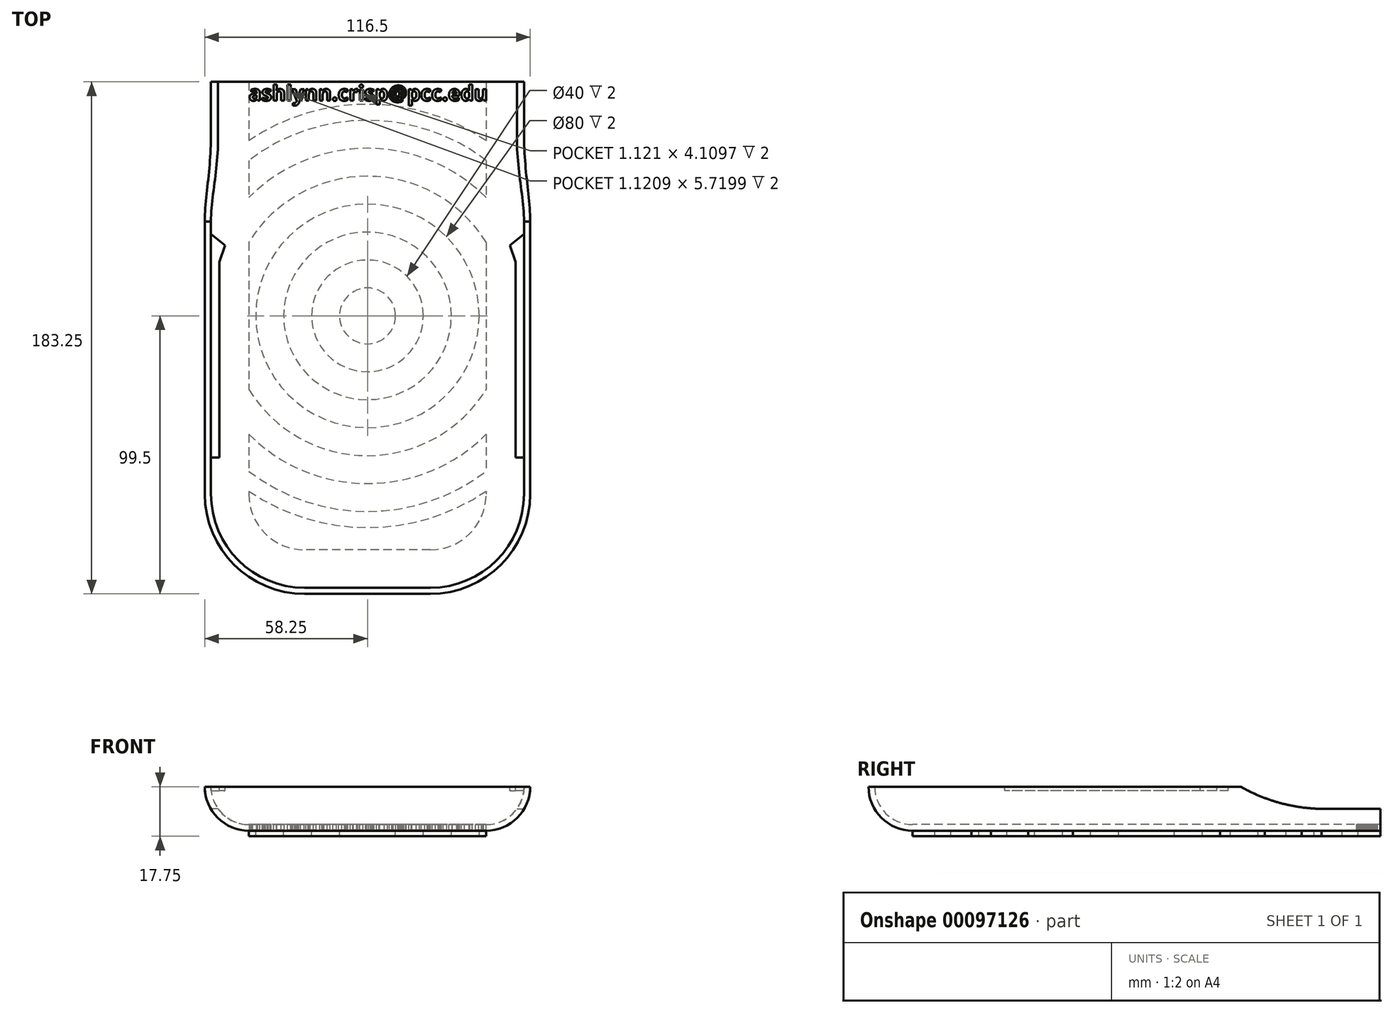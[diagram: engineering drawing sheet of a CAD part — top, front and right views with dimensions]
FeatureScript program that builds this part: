
annotation { "Feature Type Name" : "Feature", "Feature Type Description" : "" }
export const myFeature = defineFeature(function(context is Context, id is Id, definition is map)
    precondition{}
    {
        {
            var Q0;
            Q0=qCreatedBy(makeId("Right.planeOp"),FACE);
            var sketch = newSketch(context, id + "F0", { "sketchPlane" : qUnion([Q0])});
            skArc(sketch, "E0", {"start": v(-33.55, 13.55) * mm, "mid": v(-29.58, 3.97) * mm, "end": v(-20, 0) * mm});
            skArc(sketch, "E1", {"start": v(-35.75, 13.55) * mm, "mid": v(-31.14, 2.41) * mm, "end": v(-20, -2.2) * mm});
            skLineSegment(sketch, "E2", {"start": v(0, 0) * mm, "end": v(0, -24.6) * mm, "construction": true});
            skLineSegment(sketch, "E3", {"start": v(-35.75, 13.55) * mm, "end": v(-33.55, 13.55) * mm});
            skLineSegment(sketch, "E4", {"start": v(-20, 0) * mm, "end": v(-20, -2.2) * mm});
            skLineSegment(sketch, "E5", {"start": v(-29.58, 3.97) * mm, "end": v(-31.14, 2.41) * mm, "construction": true});
            skSolve(sketch);
        }
        {
            var Q0;
            Q0=makeQuery(id+"F0.imprint","IMPRINT",FACE,{"disambiguationData":[TD([[makeQuery(id+"F0.imprint","IMPRINT",EDGE,{"derivedFrom":sQuery(id+"F0.wireOp",EDGE,"E0")}),-1.0]])]});
            var Q1;
            Q1=sQuery(id+"F0.wireOp",EDGE,"E2");
            revolve(context, id + "F1", {"entities" : qUnion([Q0]), "axis" : qUnion([Q1]), "revolveType" : RevolveType.ONE_DIRECTION, "angle" : 90 * degree});
        }
        {
            var Q0;
            Q0=makeQuery(id+"F1.opRevolve","CAP_FACE",FACE,{"disambiguationData":[OSD([sQuery(id+"F0.wireOp",EDGE,"E0"),sQuery(id+"F0.wireOp",EDGE,"E1"),sQuery(id+"F0.wireOp",EDGE,"E3"),sQuery(id+"F0.wireOp",EDGE,"E4")])],"isStart":false});
            extrude(context, id + "F2", {"entities" : qUnion([Q0]), "operationType" : NewBodyOperationType.ADD, "depth" : 147.5 * mm});
        }
        {
            var Q0;
            Q0=makeQuery(id+"F1.opRevolve","CAP_FACE",FACE,{"disambiguationData":[OSD([sQuery(id+"F0.wireOp",EDGE,"E0"),sQuery(id+"F0.wireOp",EDGE,"E1"),sQuery(id+"F0.wireOp",EDGE,"E3"),sQuery(id+"F0.wireOp",EDGE,"E4")])],"isStart":true});
            extrude(context, id + "F3", {"entities" : qUnion([Q0]), "operationType" : NewBodyOperationType.ADD, "depth" : 22.5 * mm});
        }
        {
            var Q0;
            Q0=makeQuery(id+"F2.opExtrude","SWEPT_FACE",FACE,{"disambiguationData":[OSD([sQuery(id+"F0.wireOp",EDGE,"E4")])]});
            var Q1;
            Q1=makeQuery(id+"F3.opExtrude","CAP_FACE",FACE,{"disambiguationData":[OSD([sQuery(id+"F0.wireOp",EDGE,"E0"),sQuery(id+"F0.wireOp",EDGE,"E1"),sQuery(id+"F0.wireOp",EDGE,"E3"),sQuery(id+"F0.wireOp",EDGE,"E4")])],"isStart":false});
            extrude(context, id + "F4", {"entities" : qUnion([Q0]), "operationType" : NewBodyOperationType.ADD, "endBound" : BoundingType.UP_TO_SURFACE, "endBoundEntityFace" : qUnion([Q1]), "depth" : 25 * mm});
        }
        {
            var Q0;
            {var subQ0=sQuery(id+"F0.wireOp",EDGE,"E4");Q0=makeQuery(id+"F4.opExtrude","SWEPT_FACE",FACE,{"disambiguationData":[OSD([subQ0]),TDD([makeQuery(id+"F2.boolean.opBoolean","MERGE",EDGE,{"derivedFrom":[makeQuery(id+"F1.opRevolve","CAP_EDGE",EDGE,{"disambiguationData":[OSD([subQ0])],"isStart":false}),makeQuery(id+"F2.opExtrude","CAP_EDGE",EDGE,{"disambiguationData":[OSD([subQ0])],"isStart":true})]})])]});}
            var Q1;
            Q1=makeQuery(id+"F1.opRevolve","SWEPT_BODY",BODY,{"disambiguationData":[OSD([sQuery(id+"F0.wireOp",EDGE,"E0"),sQuery(id+"F0.wireOp",EDGE,"E1"),sQuery(id+"F0.wireOp",EDGE,"E3"),sQuery(id+"F0.wireOp",EDGE,"E4")])]});
            extrude(context, id + "F5", {"entities" : qUnion([Q0]), "operationType" : NewBodyOperationType.ADD, "endBound" : BoundingType.UP_TO_BODY, "endBoundEntityBody" : qUnion([Q1]), "depth" : 25 * mm});
        }
        {
            var Q0;
            Q0=makeQuery(id+"F2.opExtrude","SWEPT_EDGE",EDGE,{"disambiguationData":[OSD([sQuery(id+"F0.wireOp",EDGE,"E1"),sQuery(id+"F0.wireOp",EDGE,"E3")])]});
            cPlane(context, id + "F6", {"entities" : qUnion([Q0]), "cplaneType" : CPlaneType.LINE_ANGLE, "offset" : 150 * mm, "angle" : 90 * degree, "width" : 150 * mm, "height" : 150 * mm});
        }
        {
            var Q0;
            Q0=qCreatedBy(id+"F6.planeOp",FACE);
            var sketch = newSketch(context, id + "F7", { "sketchPlane" : qUnion([Q0])});
            skLineSegment(sketch, "E6.0", {"start": v(147.5, 13.55) * mm, "end": v(0, 13.55) * mm});
            skLineSegment(sketch, "E7.0", {"start": v(147.5, 13.55) * mm, "end": v(147.5, -2.2) * mm});
            skLineSegment(sketch, "E8.0", {"start": v(147.5, -2.2) * mm, "end": v(0, -2.2) * mm});
            skArc(sketch, "E9", {"start": v(97.5, 13.55) * mm, "mid": v(111.98, 7.62) * mm, "end": v(127.5, 5.6) * mm});
            skLineSegment(sketch, "E10", {"start": v(147.5, 5.6) * mm, "end": v(127.5, 5.6) * mm});
            skPoint(sketch, "E11", {"position": v(147.5, 5.68) * mm});
            skSolve(sketch);
        }
        {
            var Q0;
            {var subQ3=sQuery(id+"F7.wireOp",EDGE,"E9");Q0=makeQuery(id+"F7.imprint","IMPRINT",FACE,{"disambiguationData":[TD([[makeQuery(id+"F7.imprint","IMPRINT",EDGE,{"derivedFrom":subQ3}),1.0]])]});}
            var Q1;
            Q1=makeQuery(id+"F2.opExtrude","SWEPT_FACE",FACE,{"disambiguationData":[OSD([sQuery(id+"F0.wireOp",EDGE,"E0")])]});
            var Q2;
            Q2=makeQuery(id+"F1.opRevolve","SWEPT_BODY",BODY,{"disambiguationData":[OSD([sQuery(id+"F0.wireOp",EDGE,"E0"),sQuery(id+"F0.wireOp",EDGE,"E1"),sQuery(id+"F0.wireOp",EDGE,"E3"),sQuery(id+"F0.wireOp",EDGE,"E4")])]});
            extrude(context, id + "F8", {"entities" : qUnion([Q0]), "operationType" : NewBodyOperationType.REMOVE, "endBound" : BoundingType.THROUGH_ALL, "endBoundEntityFace" : qUnion([Q1]), "endBoundEntityBody" : qUnion([Q2]), "depth" : 25 * mm});
        }
        {
            var Q0;
            Q0=makeQuery(id+"F1.opRevolve","SWEPT_BODY",BODY,{"disambiguationData":[OSD([sQuery(id+"F0.wireOp",EDGE,"E0"),sQuery(id+"F0.wireOp",EDGE,"E1"),sQuery(id+"F0.wireOp",EDGE,"E3"),sQuery(id+"F0.wireOp",EDGE,"E4")])]});
            var Q1;
            {var subQ0=sQuery(id+"F0.wireOp",EDGE,"E4");var subQ1=sQuery(id+"F0.wireOp",EDGE,"E3");var subQ2=sQuery(id+"F0.wireOp",EDGE,"E1");var subQ3=sQuery(id+"F0.wireOp",EDGE,"E0");Q1=makeQuery(id+"F5.boolean.opBoolean","MERGE",FACE,{"derivedFrom":[makeQuery(id+"F3.opExtrude","CAP_FACE",FACE,{"disambiguationData":[OSD([subQ3,subQ2,subQ1,subQ0])],"isStart":false}),makeQuery(id+"F4.opExtrude","CAP_FACE",FACE,{"disambiguationData":[OSD([subQ3,subQ2,subQ1,subQ0])],"isStart":false}),makeQuery(id+"F5.opExtrude","SWEPT_FACE",FACE,{"disambiguationData":[OSD([subQ3,subQ2,subQ1,subQ0])]})]});}
            mirror(context, id + "F9", {"operationType" : NewBodyOperationType.ADD, "entities" : qUnion([Q0]), "mirrorPlane" : qUnion([Q1])});
        }
        {
            var Q0;
            {var subQ0=sQuery(id+"F0.wireOp",EDGE,"E4");var subQ1=sQuery(id+"F0.wireOp",EDGE,"E1");var subQ2=makeQuery(id+"F5.boolean.opBoolean","MERGE",FACE,{"derivedFrom":[makeQuery(id+"F4.opExtrude","SWEPT_FACE",FACE,{"disambiguationData":[OSD([subQ1,subQ0])]}),makeQuery(id+"F5.opExtrude","SWEPT_FACE",FACE,{"disambiguationData":[OSD([subQ1,subQ0])]})]});Q0=makeQuery(id+"F9.boolean.opBoolean","MERGE",FACE,{"derivedFrom":[subQ2,makeQuery(id+"F9.opPattern","COPY",FACE,{"derivedFrom":subQ2,"instanceName":"1"})]});}
            var sketch = newSketch(context, id + "F10", { "sketchPlane" : qUnion([Q0])});
            skPoint(sketch, "E12", {"position": v(22.5, -63.75) * mm});
            skCircle(sketch, "E13", {"center": v(22.5, -63.75) * mm, "radius": 10 * mm});
            skCircle(sketch, "E14", {"center": v(22.5, -63.75) * mm, "radius": 20 * mm});
            skCircle(sketch, "E15", {"center": v(22.5, -63.75) * mm, "radius": 30 * mm});
            skCircle(sketch, "E16", {"center": v(22.5, -63.75) * mm, "radius": 40 * mm});
            skArc(sketch, "E17", {"start": v(-20, -90.09) * mm, "mid": v(22.5, -113.75) * mm, "end": v(65, -90.09) * mm});
            skArc(sketch, "E18", {"start": v(-20, -106.1) * mm, "mid": v(22.5, -123.75) * mm, "end": v(65, -106.1) * mm});
            skLineSegment(sketch, "E19", {"start": v(32.5, -63.75) * mm, "end": v(12.5, -63.75) * mm, "construction": true});
            skLineSegment(sketch, "E20", {"start": v(32.5, -63.75) * mm, "end": v(42.5, -63.75) * mm, "construction": true});
            skLineSegment(sketch, "E21", {"start": v(42.5, -63.75) * mm, "end": v(52.5, -63.75) * mm, "construction": true});
            skLineSegment(sketch, "E22", {"start": v(52.5, -63.75) * mm, "end": v(62.5, -63.75) * mm, "construction": true});
            skLineSegment(sketch, "E23", {"start": v(62.5, -63.75) * mm, "end": v(72.5, -63.75) * mm, "construction": true});
            skLineSegment(sketch, "E24", {"start": v(72.5, -63.75) * mm, "end": v(82.5, -63.75) * mm, "construction": true});
            skArc(sketch, "E25", {"start": v(-20, -119.37) * mm, "mid": v(22.5, -133.75) * mm, "end": v(65, -119.37) * mm});
            skLineSegment(sketch, "E26", {"start": v(82.5, -63.75) * mm, "end": v(92.5, -63.75) * mm, "construction": true});
            skLineSegment(sketch, "E27", {"start": v(92.5, -63.75) * mm, "end": v(102.5, -63.75) * mm, "construction": true});
            skLineSegment(sketch, "E28", {"start": v(102.5, -63.75) * mm, "end": v(112.5, -63.75) * mm, "construction": true});
            skLineSegment(sketch, "E29", {"start": v(112.5, -63.75) * mm, "end": v(122.5, -63.75) * mm, "construction": true});
            skLineSegment(sketch, "E30.0.0", {"start": v(-20, -147.5) * mm, "end": v(65, -147.5) * mm});
            skLineSegment(sketch, "E30.0.1", {"start": v(65, -147.5) * mm, "end": v(65, 0) * mm});
            skArc(sketch, "E30.0.2", {"start": v(65, 0) * mm, "mid": v(59.14, 14.14) * mm, "end": v(45, 20) * mm});
            skLineSegment(sketch, "E30.0.3", {"start": v(45, 20) * mm, "end": v(0, 20) * mm});
            skArc(sketch, "E30.0.4", {"start": v(0, 20) * mm, "mid": v(-14.14, 14.14) * mm, "end": v(-20, 0) * mm});
            skLineSegment(sketch, "E30.0.5", {"start": v(-20, 0) * mm, "end": v(-20, -147.5) * mm});
            skArc(sketch, "E31.trimOffspring", {"start": v(65, -8.13) * mm, "mid": v(22.5, 6.25) * mm, "end": v(-20, -8.13) * mm});
            skArc(sketch, "E32.trimOffspring", {"start": v(65, -21.4) * mm, "mid": v(22.5, -3.75) * mm, "end": v(-20, -21.4) * mm});
            skArc(sketch, "E33.trimOffspring", {"start": v(65, -37.41) * mm, "mid": v(22.5, -13.75) * mm, "end": v(-20, -37.41) * mm});
            skArc(sketch, "E34", {"start": v(64.53, 4.32) * mm, "mid": v(22.5, 16.25) * mm, "end": v(-19.53, 4.32) * mm});
            skCircle(sketch, "E35", {"center": v(22.5, -63.75) * mm, "radius": 75.75 * mm});
            skPoint(sketch, "E36", {"position": v(22.5, -147.5) * mm});
            skPoint(sketch, "E37", {"position": v(22.5, -139.5) * mm});
            skSolve(sketch);
        }
        {
            var Q0;
            Q0=makeQuery(id+"F10.imprint","IMPRINT",FACE,{"disambiguationData":[TD([[makeQuery(id+"F10.imprint","IMPRINT",EDGE,{"derivedFrom":sQuery(id+"F10.wireOp",EDGE,"E13")}),1.0]])]});
            var Q1;
            Q1=makeQuery(id+"F10.imprint","IMPRINT",FACE,{"disambiguationData":[TD([[makeQuery(id+"F10.imprint","IMPRINT",EDGE,{"derivedFrom":sQuery(id+"F10.wireOp",EDGE,"E14")}),-1.0]])]});
            var Q2;
            Q2=makeQuery(id+"F10.imprint","IMPRINT",FACE,{"disambiguationData":[TD([[makeQuery(id+"F10.imprint","IMPRINT",EDGE,{"derivedFrom":sQuery(id+"F10.wireOp",EDGE,"E16")}),-1.0]])]});
            var Q3;
            {var subQ0=sQuery(id+"F10.wireOp",EDGE,"E31.trimOffspring");Q3=makeQuery(id+"F10.imprint","IMPRINT",FACE,{"disambiguationData":[TD([[makeQuery(id+"F10.imprint","IMPRINT",EDGE,{"derivedFrom":subQ0}),1.0]])]});}
            var Q4;
            {var subQ0=sQuery(id+"F10.wireOp",EDGE,"E18");Q4=makeQuery(id+"F10.imprint","IMPRINT",FACE,{"disambiguationData":[TD([[makeQuery(id+"F10.imprint","IMPRINT",EDGE,{"derivedFrom":subQ0}),-1.0]])]});}
            var Q5;
            {var subQ0=sQuery(id+"F10.wireOp",EDGE,"E30.0.0");Q5=makeQuery(id+"F10.imprint","IMPRINT",FACE,{"disambiguationData":[TD([[makeQuery(id+"F10.imprint","IMPRINT",EDGE,{"derivedFrom":subQ0}),-1.0]])]});}
            var Q6;
            {var subQ8=sQuery(id+"F10.wireOp",EDGE,"E34");Q6=makeQuery(id+"F10.imprint","IMPRINT",FACE,{"disambiguationData":[TD([[makeQuery(id+"F10.imprint","IMPRINT",EDGE,{"derivedFrom":subQ8}),1.0]])]});}
            var Q7;
            {var subQ0=sQuery(id+"F10.wireOp",EDGE,"E30.0.3");Q7=makeQuery(id+"F10.imprint","IMPRINT",FACE,{"disambiguationData":[TD([[makeQuery(id+"F10.imprint","IMPRINT",EDGE,{"derivedFrom":subQ0}),1.0]])]});}
            extrude(context, id + "F11", {"entities" : qUnion([Q0, Q1, Q2, Q3, Q4, Q5, Q6, Q7]), "depth" : 2 * mm});
        }
        {
            var Q0;
            {var subQ0=sQuery(id+"F0.wireOp",EDGE,"E4");var subQ1=sQuery(id+"F0.wireOp",EDGE,"E0");var subQ2=makeQuery(id+"F5.boolean.opBoolean","MERGE",FACE,{"derivedFrom":[makeQuery(id+"F4.opExtrude","SWEPT_FACE",FACE,{"disambiguationData":[OSD([subQ1,subQ0])]}),makeQuery(id+"F5.opExtrude","SWEPT_FACE",FACE,{"disambiguationData":[OSD([subQ1,subQ0])]})]});Q0=makeQuery(id+"F9.boolean.opBoolean","MERGE",FACE,{"derivedFrom":[subQ2,makeQuery(id+"F9.opPattern","COPY",FACE,{"derivedFrom":subQ2,"instanceName":"1"})]});}
            var sketch = newSketch(context, id + "F12", { "sketchPlane" : qUnion([Q0])});
            skLineSegment(sketch, "E38.0.1", {"start": v(-20, 126.45) * mm, "end": v(-20, 147.5) * mm});
            skLineSegment(sketch, "E38.0.2", {"start": v(-20, 147.5) * mm, "end": v(65, 147.5) * mm});
            skLineSegment(sketch, "E38.0.3", {"start": v(65, 147.5) * mm, "end": v(65, 126.45) * mm});
            skText(sketch, "E39", { "text": "<email>", "fontName": "OpenSans-Bold.ttf"});
            skPoint(sketch, "E40", {"position": v(22.5, 147.5) * mm});
            skPoint(sketch, "E41", {"position": v(22.5, 139.5) * mm});
            skLineSegment(sketch, "E42", {"start": v(22.5, 147.5) * mm, "end": v(22.5, 139.5) * mm, "construction": true});
            skPoint(sketch, "E43", {"position": v(22.5, 143.5) * mm});
            skArc(sketch, "E44.0.0", {"start": v(65, 126.45) * mm, "mid": v(22.5, 139.5) * mm, "end": v(-20, 126.45) * mm});
            const initialGuessF12  = {"E39": [-0.02, 0.14079, 1, 0, 0.00542]};
            skSetInitialGuess(sketch, initialGuessF12);
            skSolve(sketch);
        }
        {
            var Q0;
            Q0=makeQuery(id+"F12.imprint","IMPRINT",FACE,{"disambiguationData":[TD([[makeQuery(id+"F12.imprint","IMPRINT",EDGE,{"derivedFrom":sQuery(id+"F12.wireOp",EDGE,"E39.sketch_text.stroke-0")}),-1.0]])]});
            var Q1;
            Q1=makeQuery(id+"F12.imprint","IMPRINT",FACE,{"disambiguationData":[TD([[makeQuery(id+"F12.imprint","IMPRINT",EDGE,{"derivedFrom":sQuery(id+"F12.wireOp",EDGE,"E39.sketch_text.stroke-25")}),-1.0]])]});
            var Q2;
            Q2=makeQuery(id+"F12.imprint","IMPRINT",FACE,{"disambiguationData":[TD([[makeQuery(id+"F12.imprint","IMPRINT",EDGE,{"derivedFrom":sQuery(id+"F12.wireOp",EDGE,"E39.sketch_text.stroke-51")}),-1.0]])]});
            var Q3;
            Q3=makeQuery(id+"F12.imprint","IMPRINT",FACE,{"disambiguationData":[TD([[makeQuery(id+"F12.imprint","IMPRINT",EDGE,{"derivedFrom":sQuery(id+"F12.wireOp",EDGE,"E39.sketch_text.stroke-68")}),-1.0]])]});
            var Q4;
            Q4=makeQuery(id+"F12.imprint","IMPRINT",FACE,{"disambiguationData":[TD([[makeQuery(id+"F12.imprint","IMPRINT",EDGE,{"derivedFrom":sQuery(id+"F12.wireOp",EDGE,"E39.sketch_text.stroke-72")}),-1.0]])]});
            var Q5;
            Q5=makeQuery(id+"F12.imprint","IMPRINT",FACE,{"disambiguationData":[TD([[makeQuery(id+"F12.imprint","IMPRINT",EDGE,{"derivedFrom":sQuery(id+"F12.wireOp",EDGE,"E39.sketch_text.stroke-89")}),-1.0]])]});
            var Q6;
            Q6=makeQuery(id+"F12.imprint","IMPRINT",FACE,{"disambiguationData":[TD([[makeQuery(id+"F12.imprint","IMPRINT",EDGE,{"derivedFrom":sQuery(id+"F12.wireOp",EDGE,"E39.sketch_text.stroke-106")}),-1.0]])]});
            var Q7;
            Q7=makeQuery(id+"F12.imprint","IMPRINT",FACE,{"disambiguationData":[TD([[makeQuery(id+"F12.imprint","IMPRINT",EDGE,{"derivedFrom":sQuery(id+"F12.wireOp",EDGE,"E39.sketch_text.stroke-123")}),-1.0]])]});
            var Q8;
            Q8=makeQuery(id+"F12.imprint","IMPRINT",FACE,{"disambiguationData":[TD([[makeQuery(id+"F12.imprint","IMPRINT",EDGE,{"derivedFrom":sQuery(id+"F12.wireOp",EDGE,"E39.sketch_text.stroke-131")}),-1.0]])]});
            var Q9;
            Q9=makeQuery(id+"F12.imprint","IMPRINT",FACE,{"disambiguationData":[TD([[makeQuery(id+"F12.imprint","IMPRINT",EDGE,{"derivedFrom":sQuery(id+"F12.wireOp",EDGE,"E39.sketch_text.stroke-145")}),-1.0]])]});
            var Q10;
            Q10=makeQuery(id+"F12.imprint","IMPRINT",FACE,{"disambiguationData":[TD([[makeQuery(id+"F12.imprint","IMPRINT",EDGE,{"derivedFrom":sQuery(id+"F12.wireOp",EDGE,"E39.sketch_text.stroke-158")}),-1.0]])]});
            var Q11;
            Q11=makeQuery(id+"F12.imprint","IMPRINT",FACE,{"disambiguationData":[TD([[makeQuery(id+"F12.imprint","IMPRINT",EDGE,{"derivedFrom":sQuery(id+"F12.wireOp",EDGE,"E39.sketch_text.stroke-163")}),-1.0]])]});
            var Q12;
            Q12=makeQuery(id+"F12.imprint","IMPRINT",FACE,{"disambiguationData":[TD([[makeQuery(id+"F12.imprint","IMPRINT",EDGE,{"derivedFrom":sQuery(id+"F12.wireOp",EDGE,"E39.sketch_text.stroke-167")}),-1.0]])]});
            var Q13;
            Q13=makeQuery(id+"F12.imprint","IMPRINT",FACE,{"disambiguationData":[TD([[makeQuery(id+"F12.imprint","IMPRINT",EDGE,{"derivedFrom":sQuery(id+"F12.wireOp",EDGE,"E39.sketch_text.stroke-193")}),-1.0]])]});
            var Q14;
            Q14=makeQuery(id+"F12.imprint","IMPRINT",FACE,{"disambiguationData":[TD([[makeQuery(id+"F12.imprint","IMPRINT",EDGE,{"derivedFrom":sQuery(id+"F12.wireOp",EDGE,"E39.sketch_text.stroke-216")}),-1.0]])]});
            var Q15;
            Q15=makeQuery(id+"F12.imprint","IMPRINT",FACE,{"disambiguationData":[TD([[makeQuery(id+"F12.imprint","IMPRINT",EDGE,{"derivedFrom":sQuery(id+"F12.wireOp",EDGE,"E39.sketch_text.stroke-260")}),-1.0]])]});
            var Q16;
            Q16=makeQuery(id+"F12.imprint","IMPRINT",FACE,{"disambiguationData":[TD([[makeQuery(id+"F12.imprint","IMPRINT",EDGE,{"derivedFrom":sQuery(id+"F12.wireOp",EDGE,"E39.sketch_text.stroke-283")}),-1.0]])]});
            var Q17;
            {var subQ6=sQuery(id+"F12.wireOp",EDGE,"E39.sketch_text.stroke-362");Q17=makeQuery(id+"F12.imprint","IMPRINT",FACE,{"disambiguationData":[TD([[makeQuery(id+"F12.imprint","IMPRINT",EDGE,{"derivedFrom":subQ6}),-1.0]])]});}
            var Q18;
            Q18=makeQuery(id+"F12.imprint","IMPRINT",FACE,{"disambiguationData":[TD([[makeQuery(id+"F12.imprint","IMPRINT",EDGE,{"derivedFrom":sQuery(id+"F12.wireOp",EDGE,"E39.sketch_text.stroke-297")}),-1.0]])]});
            var Q19;
            Q19=makeQuery(id+"F12.imprint","IMPRINT",FACE,{"disambiguationData":[TD([[makeQuery(id+"F12.imprint","IMPRINT",EDGE,{"derivedFrom":sQuery(id+"F12.wireOp",EDGE,"E39.sketch_text.stroke-319")}),-1.0]])]});
            var Q20;
            Q20=makeQuery(id+"F12.imprint","IMPRINT",FACE,{"disambiguationData":[TD([[makeQuery(id+"F12.imprint","IMPRINT",EDGE,{"derivedFrom":sQuery(id+"F12.wireOp",EDGE,"E39.sketch_text.stroke-339")}),-1.0]])]});
            var Q21;
            Q21=makeQuery(id+"F12.imprint","IMPRINT",FACE,{"disambiguationData":[TD([[makeQuery(id+"F12.imprint","IMPRINT",EDGE,{"derivedFrom":sQuery(id+"F12.wireOp",EDGE,"E39.sketch_text.stroke-311")}),-1.0]])]});
            extrude(context, id + "F13", {"entities" : qUnion([Q0, Q1, Q2, Q3, Q4, Q5, Q6, Q7, Q8, Q9, Q10, Q11, Q12, Q13, Q14, Q15, Q16, Q17, Q18, Q19, Q20, Q21]), "operationType" : NewBodyOperationType.REMOVE, "oppositeDirection" : true, "depth" : 2 * mm});
        }
        {
            var Q0;
            {var subQ0=sQuery(id+"F0.wireOp",EDGE,"E3");var subQ1=makeQuery(id+"F3.boolean.opBoolean","MERGE",FACE,{"derivedFrom":[makeQuery(id+"F2.boolean.opBoolean","MERGE",FACE,{"derivedFrom":[makeQuery(id+"F1.opRevolve","SWEPT_FACE",FACE,{"disambiguationData":[OSD([subQ0])]}),makeQuery(id+"F2.opExtrude","SWEPT_FACE",FACE,{"disambiguationData":[OSD([subQ0])]})]}),makeQuery(id+"F3.opExtrude","SWEPT_FACE",FACE,{"disambiguationData":[OSD([subQ0])]})]});Q0=makeQuery(id+"F9.boolean.opBoolean","MERGE",FACE,{"derivedFrom":[subQ1,makeQuery(id+"F9.opPattern","COPY",FACE,{"derivedFrom":subQ1,"instanceName":"1"})]});}
            var sketch = newSketch(context, id + "F14", { "sketchPlane" : qUnion([Q0])});
            skFitSpline(sketch, "E45.0.0", {"points": [v(-30.97, 127.5) * mm, v(-30.97, 126.2) * mm, v(-31, 124.88) * mm, v(-31.06, 123.55) * mm, v(-31.12, 122.3) * mm, v(-31.2, 121) * mm, v(-31.33, 119.65) * mm, v(-31.43, 118.45) * mm, v(-31.56, 117.16) * mm, v(-31.72, 115.78) * mm, v(-31.84, 114.73) * mm, v(-32, 113.45) * mm, v(-32.19, 111.95) * mm, v(-32.22, 111.69) * mm, v(-32.3, 111.06) * mm, v(-32.43, 110.07) * mm, v(-32.53, 109.3) * mm, v(-32.61, 108.69) * mm, v(-32.67, 108.21) * mm, v(-32.85, 106.8) * mm, v(-33, 105.58) * mm, v(-33.1, 104.56) * mm, v(-33.25, 103.26) * mm, v(-33.35, 102.07) * mm, v(-33.42, 101) * mm, v(-33.5, 99.74) * mm, v(-33.55, 98.57) * mm, v(-33.55, 97.5) * mm]});
            skLineSegment(sketch, "E45.0.1", {"start": v(-33.55, 97.5) * mm, "end": v(-33.55, 0) * mm});
            skLineSegment(sketch, "E45.0.2", {"start": v(-33.55, 0) * mm, "end": v(-20, 0) * mm});
            skLineSegment(sketch, "E45.0.3", {"start": v(-20, 0) * mm, "end": v(-20, 147.5) * mm});
            skLineSegment(sketch, "E45.0.4", {"start": v(-20, 147.5) * mm, "end": v(-30.97, 147.5) * mm});
            skLineSegment(sketch, "E45.0.5", {"start": v(-30.97, 147.5) * mm, "end": v(-30.97, 127.5) * mm});
            skLineSegment(sketch, "E46.0", {"start": v(-35.75, 97.5) * mm, "end": v(-35.75, 0) * mm});
            skArc(sketch, "E47.0", {"start": v(-35.75, 0) * mm, "mid": v(-25.28, -25.28) * mm, "end": v(0, -35.75) * mm});
            skLineSegment(sketch, "E48.0", {"start": v(78.55, 97.5) * mm, "end": v(78.55, 0) * mm});
            skFitSpline(sketch, "E49.0", {"points": [v(80.75, 97.5) * mm, v(80.75, 98.57) * mm, v(80.71, 99.73) * mm, v(80.64, 100.99) * mm, v(80.58, 102.06) * mm, v(80.5, 103.25) * mm, v(80.37, 104.56) * mm, v(80.28, 105.56) * mm, v(80.16, 106.78) * mm, v(80, 108.22) * mm, v(79.96, 108.64) * mm, v(79.89, 109.26) * mm, v(79.8, 110.09) * mm, v(79.7, 110.93) * mm, v(79.64, 111.56) * mm, v(79.6, 111.98) * mm, v(79.43, 113.45) * mm, v(79.3, 114.72) * mm, v(79.2, 115.8) * mm, v(79.07, 117.17) * mm, v(78.97, 118.46) * mm, v(78.88, 119.66) * mm, v(78.79, 121) * mm, v(78.72, 122.3) * mm, v(78.67, 123.56) * mm, v(78.62, 124.89) * mm, v(78.6, 126.2) * mm, v(78.6, 127.5) * mm]});
            skLineSegment(sketch, "E50.bottom", {"start": v(-33.55, 83) * mm, "end": v(-30.55, 83) * mm});
            skLineSegment(sketch, "E50.top", {"start": v(-33.55, 13) * mm, "end": v(-30.55, 13) * mm});
            skLineSegment(sketch, "E50.left", {"start": v(-33.55, 83) * mm, "end": v(-33.55, 13) * mm});
            skLineSegment(sketch, "E50.right", {"start": v(-30.55, 83) * mm, "end": v(-30.55, 13) * mm});
            skPoint(sketch, "E51.0", {"position": v(5.37, 144.9) * mm});
            skLineSegment(sketch, "E52.0", {"start": v(65, 147.5) * mm, "end": v(-20, 147.5) * mm});
            skPoint(sketch, "E53", {"position": v(22.5, 147.5) * mm});
            skLineSegment(sketch, "E54", {"start": v(22.5, 147.5) * mm, "end": v(22.5, -20) * mm, "construction": true});
            skLineSegment(sketch, "E55", {"start": v(-33.55, 93) * mm, "end": v(-28.55, 89) * mm});
            skLineSegment(sketch, "E56", {"start": v(-28.55, 89) * mm, "end": v(-30.55, 83) * mm});
            skLineSegment(sketch, "E57", {"start": v(-28.55, 89) * mm, "end": v(-33.55, 89) * mm});
            skSolve(sketch);
        }
        {
            var Q0;
            Q0=makeQuery(id+"F14.imprint","IMPRINT",FACE,{"disambiguationData":[TD([[makeQuery(id+"F14.imprint","IMPRINT",EDGE,{"derivedFrom":sQuery(id+"F14.wireOp",EDGE,"E50.bottom")}),-1.0]])]});
            var Q1;
            {var subQ0=sQuery(id+"F14.wireOp",EDGE,"E50.bottom");Q1=makeQuery(id+"F14.imprint","IMPRINT",FACE,{"disambiguationData":[TD([[makeQuery(id+"F14.imprint","IMPRINT",EDGE,{"derivedFrom":subQ0}),1.0]])]});}
            var Q2;
            {var subQ0=sQuery(id+"F14.wireOp",EDGE,"E55");Q2=makeQuery(id+"F14.imprint","IMPRINT",FACE,{"disambiguationData":[TD([[makeQuery(id+"F14.imprint","IMPRINT",EDGE,{"derivedFrom":subQ0}),-1.0]])]});}
            extrude(context, id + "F15", {"entities" : qUnion([Q0, Q1, Q2]), "oppositeDirection" : true, "depth" : 1.5 * mm});
        }
        {
            var Q0;
            Q0=sQuery(id+"F14.wireOp",EDGE,"E54");
            cPlane(context, id + "F16", {"entities" : qUnion([Q0]), "cplaneType" : CPlaneType.LINE_ANGLE, "offset" : 150 * mm, "angle" : 90 * degree, "width" : 150 * mm, "height" : 150 * mm});
        }
        {
            var Q0;
            Q0=makeQuery(id+"F15.opExtrude","SWEPT_BODY",BODY,{"disambiguationData":[OSD([sQuery(id+"F14.wireOp",EDGE,"E45.0.1"),sQuery(id+"F14.wireOp",EDGE,"E50.top"),sQuery(id+"F14.wireOp",EDGE,"E50.left"),sQuery(id+"F14.wireOp",EDGE,"E50.right"),sQuery(id+"F14.wireOp",EDGE,"E55"),sQuery(id+"F14.wireOp",EDGE,"E56")])]});
            var Q1;
            Q1=qCreatedBy(id+"F16.planeOp",FACE);
            mirror(context, id + "F17", {"entities" : qUnion([Q0]), "mirrorPlane" : qUnion([Q1])});
        }
    });
